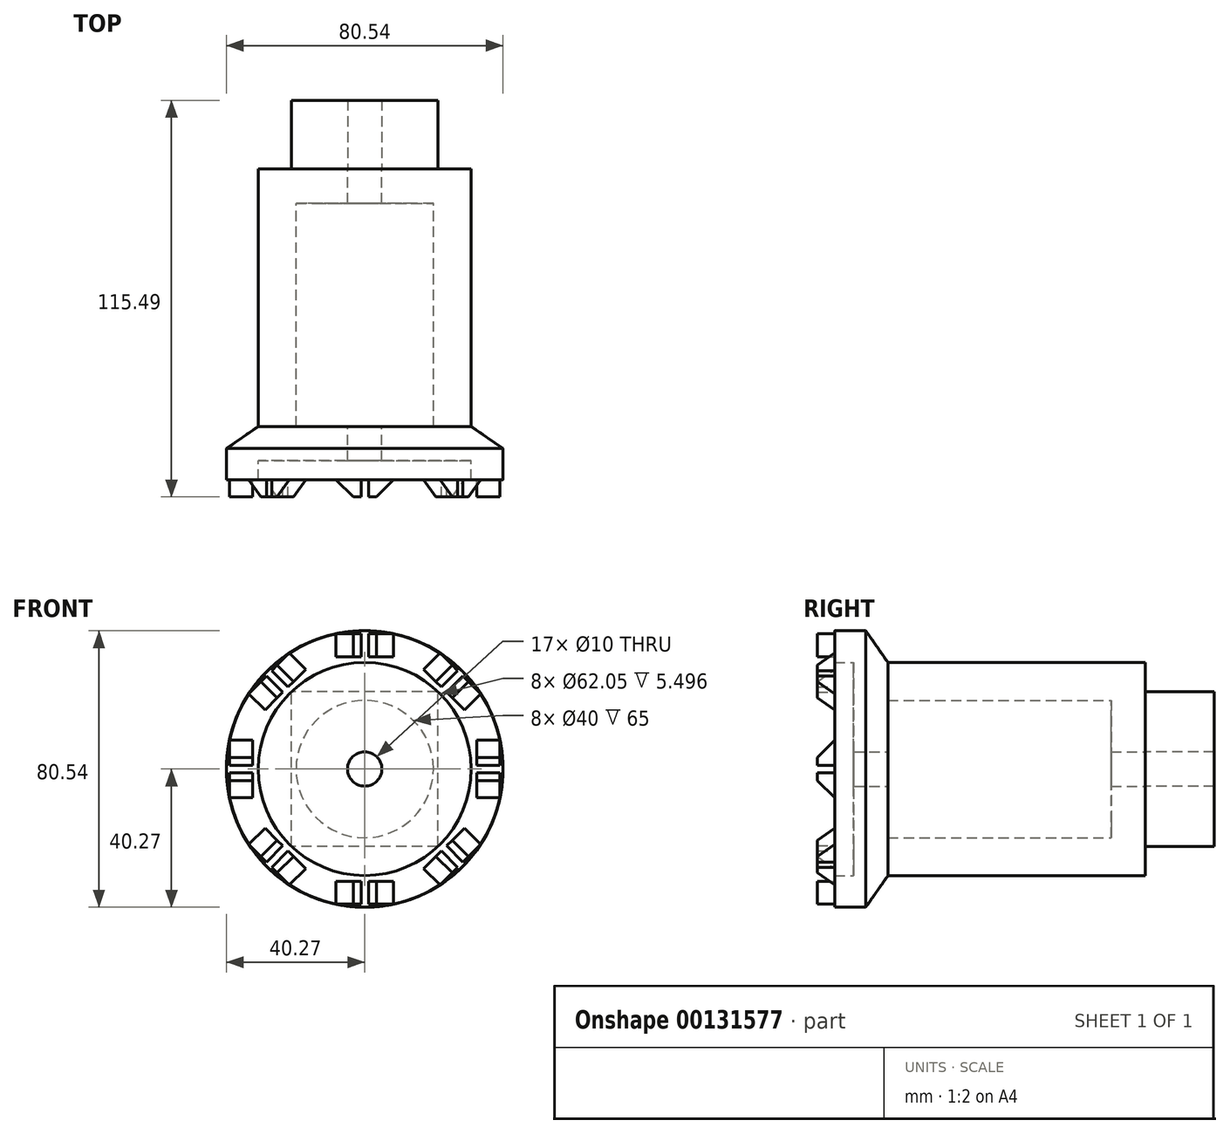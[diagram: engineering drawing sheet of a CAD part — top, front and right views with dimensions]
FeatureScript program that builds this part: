
annotation { "Feature Type Name" : "Feature", "Feature Type Description" : "" }
export const myFeature = defineFeature(function(context is Context, id is Id, definition is map)
    precondition{}
    {
        {
            var Q0;
            Q0=qCreatedBy(makeId("Right.planeOp"),FACE);
            var sketch = newSketch(context, id + "F0", { "sketchPlane" : qUnion([Q0])});
            skLineSegment(sketch, "E0.bottom", {"start": v(60, 5) * mm, "end": v(-60, 5) * mm});
            skLineSegment(sketch, "E0.top", {"start": v(60, -5) * mm, "end": v(-60, -5) * mm});
            skLineSegment(sketch, "E0.left", {"start": v(60, 5) * mm, "end": v(60, -5) * mm});
            skLineSegment(sketch, "E0.right", {"start": v(-60, 5) * mm, "end": v(-60, -5) * mm});
            skPoint(sketch, "E0.middle", {"position": v(0, 0) * mm});
            skLineSegment(sketch, "E1", {"start": v(45.53, 5) * mm, "end": v(45.53, 20) * mm});
            skLineSegment(sketch, "E2", {"start": v(45.53, 20) * mm, "end": v(-19.47, 20) * mm});
            skLineSegment(sketch, "E3", {"start": v(-19.47, 20) * mm, "end": v(-19.47, 5) * mm});
            skLineSegment(sketch, "E4", {"start": v(-19.47, 5) * mm, "end": v(-29.47, 5) * mm});
            skLineSegment(sketch, "E5", {"start": v(-29.47, 5) * mm, "end": v(-29.47, 31.03) * mm});
            skLineSegment(sketch, "E6", {"start": v(-34.96, 40.27) * mm, "end": v(-25.88, 40.27) * mm});
            skLineSegment(sketch, "E7", {"start": v(-19.47, 31.03) * mm, "end": v(-25.88, 40.27) * mm});
            skLineSegment(sketch, "E8", {"start": v(-19.47, 31.03) * mm, "end": v(55.53, 31.03) * mm});
            skLineSegment(sketch, "E9", {"start": v(55.53, 31.03) * mm, "end": v(55.53, 5) * mm});
            skLineSegment(sketch, "E10", {"start": v(70.6, 0) * mm, "end": v(-73.15, 0) * mm});
            skLineSegment(sketch, "E11", {"start": v(-29.47, 31.03) * mm, "end": v(-34.96, 31.03) * mm});
            skLineSegment(sketch, "E12", {"start": v(-34.96, 31.03) * mm, "end": v(-34.96, 40.27) * mm});
            skSolve(sketch);
        }
        {
            var Q0;
            {var subQ0=sQuery(id+"F0.wireOp",EDGE,"E1");Q0=makeQuery(id+"F0.imprint","IMPRINT",FACE,{"disambiguationData":[TD([[makeQuery(id+"F0.imprint","IMPRINT",EDGE,{"derivedFrom":subQ0}),-1.0]])]});}
            var Q1;
            Q1=sQuery(id+"F0.wireOp",EDGE,"E10");
            revolve(context, id + "F1", {"entities" : qUnion([Q0]), "axis" : qUnion([Q1]), "revolveType" : RevolveType.FULL});
        }
        {
            var Q0;
            Q0=makeQuery(id+"F1.opRevolve","SWEPT_FACE",FACE,{"disambiguationData":[OSD([sQuery(id+"F0.wireOp",EDGE,"E12")])]});
            var sketch = newSketch(context, id + "F2", { "sketchPlane" : qUnion([Q0])});
            skLineSegment(sketch, "E13.bottom", {"start": v(8.36, 39.4) * mm, "end": v(-8.36, 39.4) * mm});
            skLineSegment(sketch, "E13.top", {"start": v(8.36, 32.7) * mm, "end": v(-8.36, 32.7) * mm});
            skLineSegment(sketch, "E13.left", {"start": v(8.36, 39.4) * mm, "end": v(8.36, 32.7) * mm});
            skLineSegment(sketch, "E13.right", {"start": v(-8.36, 39.4) * mm, "end": v(-8.36, 32.7) * mm});
            skPoint(sketch, "E13.middle", {"position": v(0, 36.04) * mm});
            skLineSegment(sketch, "E14.bottom", {"start": v(-1.08, 39.4) * mm, "end": v(1.08, 39.4) * mm});
            skLineSegment(sketch, "E14.top", {"start": v(-1.08, 32.7) * mm, "end": v(1.08, 32.7) * mm});
            skLineSegment(sketch, "E14.left", {"start": v(-1.08, 39.4) * mm, "end": v(-1.08, 32.7) * mm});
            skLineSegment(sketch, "E14.right", {"start": v(1.08, 39.4) * mm, "end": v(1.08, 32.7) * mm});
            skSolve(sketch);
        }
        {
            var Q0;
            {var subQ0=sQuery(id+"F2.wireOp",EDGE,"E13.left");Q0=makeQuery(id+"F2.imprint","IMPRINT",FACE,{"disambiguationData":[TD([[makeQuery(id+"F2.imprint","IMPRINT",EDGE,{"derivedFrom":subQ0}),-1.0]])]});}
            var Q1;
            {var subQ0=sQuery(id+"F2.wireOp",EDGE,"E13.right");Q1=makeQuery(id+"F2.imprint","IMPRINT",FACE,{"disambiguationData":[TD([[makeQuery(id+"F2.imprint","IMPRINT",EDGE,{"derivedFrom":subQ0}),1.0]])]});}
            extrude(context, id + "F3", {"entities" : qUnion([Q0, Q1]), "operationType" : NewBodyOperationType.ADD, "depth" : 5 * mm});
        }
        {
            var Q0;
            Q0=makeQuery(id+"F3.opExtrude","CAP_EDGE",EDGE,{"disambiguationData":[OSD([sQuery(id+"F2.wireOp",EDGE,"E13.right")])],"isStart":false});
            var Q1;
            Q1=makeQuery(id+"F3.opExtrude","CAP_EDGE",EDGE,{"disambiguationData":[OSD([sQuery(id+"F2.wireOp",EDGE,"E13.left")])],"isStart":false});
            chamfer(context, id + "F4", {"entities" : qUnion([Q0, Q1]), "width" : 5 * mm, "tangentPropagation" : true});
        }
        {
            var Q0;
            Q0=makeQuery(id+"F1.opRevolve","SWEPT_BODY",BODY,{"disambiguationData":[OSD([sQuery(id+"F0.wireOp",EDGE,"E0.bottom"),sQuery(id+"F0.wireOp",EDGE,"E1"),sQuery(id+"F0.wireOp",EDGE,"E2"),sQuery(id+"F0.wireOp",EDGE,"E3"),sQuery(id+"F0.wireOp",EDGE,"E4"),sQuery(id+"F0.wireOp",EDGE,"E5"),sQuery(id+"F0.wireOp",EDGE,"E6"),sQuery(id+"F0.wireOp",EDGE,"E7"),sQuery(id+"F0.wireOp",EDGE,"E8"),sQuery(id+"F0.wireOp",EDGE,"E9"),sQuery(id+"F0.wireOp",EDGE,"E11"),sQuery(id+"F0.wireOp",EDGE,"E12")])]});
            var Q1;
            Q1=sQuery(id+"F0.wireOp",EDGE,"E10");
            circularPattern(context, id + "F5", {"entities" : qUnion([Q0]), "axis" : qUnion([Q1]), "angle" : 360 * degree, "instanceCount" : 8, "equalSpace" : true});
        }
        {
            var Q0;
            Q0=makeQuery(id+"F1.opRevolve","SWEPT_FACE",FACE,{"disambiguationData":[OSD([sQuery(id+"F0.wireOp",EDGE,"E9")])]});
            var sketch = newSketch(context, id + "F6", { "sketchPlane" : qUnion([Q0])});
            skLineSegment(sketch, "E15.bottom", {"start": v(-21.33, -22.53) * mm, "end": v(21.33, -22.53) * mm});
            skLineSegment(sketch, "E15.top", {"start": v(-21.33, 22.53) * mm, "end": v(21.33, 22.53) * mm});
            skLineSegment(sketch, "E15.left", {"start": v(-21.33, -22.53) * mm, "end": v(-21.33, 22.53) * mm});
            skLineSegment(sketch, "E15.right", {"start": v(21.33, -22.53) * mm, "end": v(21.33, 22.53) * mm});
            skSolve(sketch);
        }
        {
            var Q0;
            Q0=makeQuery(id+"F6.imprint","IMPRINT",FACE,{"disambiguationData":[TD([[makeQuery(id+"F6.imprint","IMPRINT",EDGE,{"derivedFrom":sQuery(id+"F6.wireOp",EDGE,"E15.bottom")}),1.0]])]});
            extrude(context, id + "F7", {"entities" : qUnion([Q0]), "depth" : 20 * mm});
        }
    });
